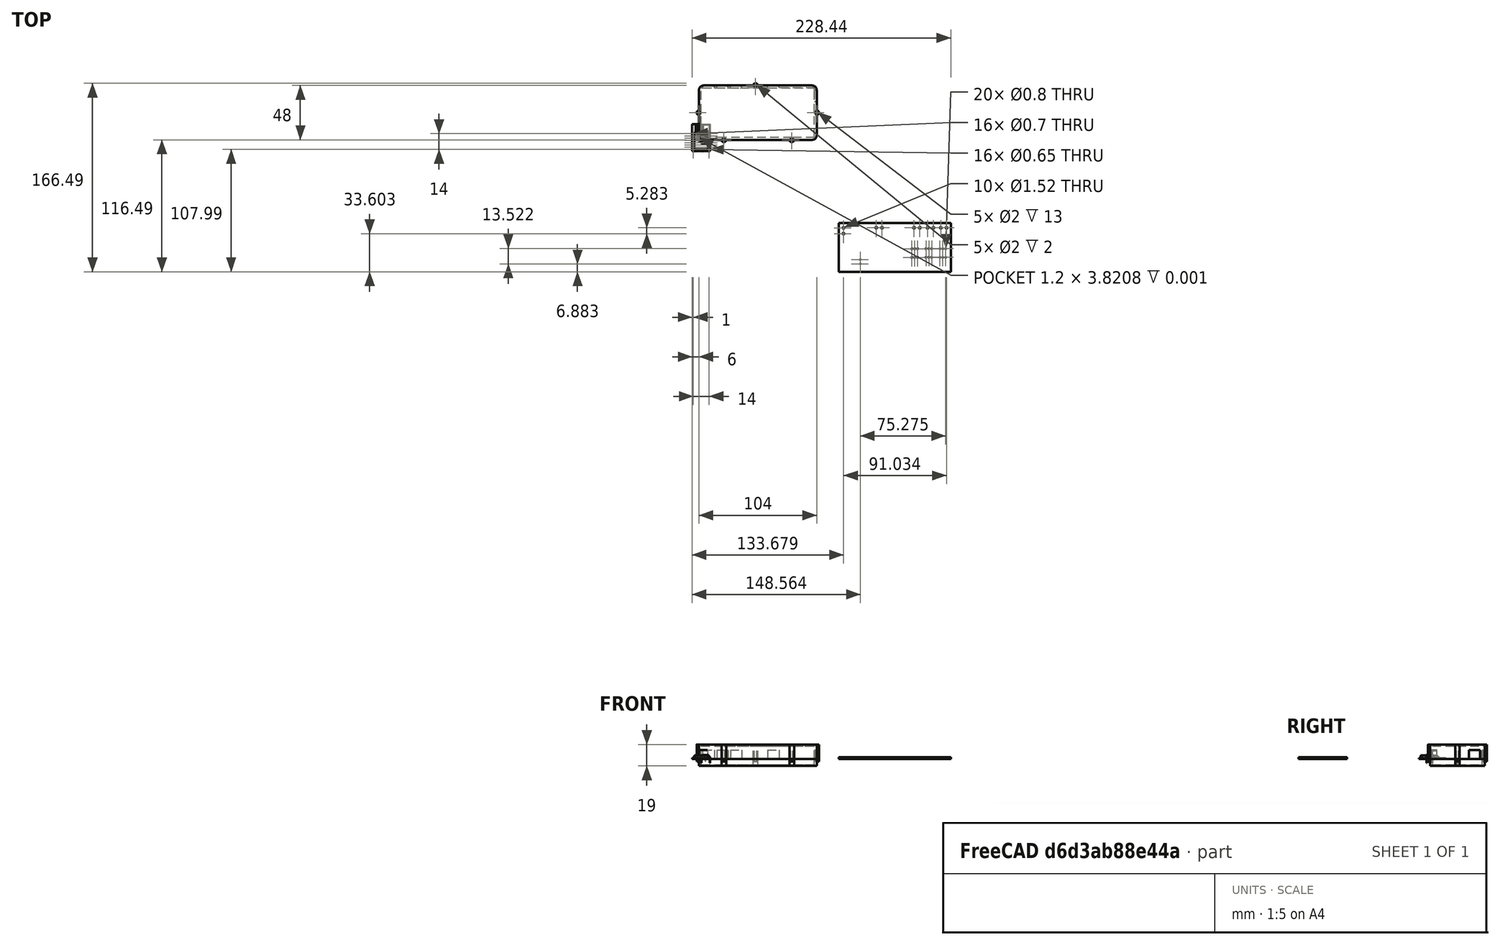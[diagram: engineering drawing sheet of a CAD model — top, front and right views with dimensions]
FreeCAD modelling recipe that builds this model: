
FCSTD DOCUMENT  (FreeCAD 0.20R29603 (Git))
Label: box
License: All rights reserved
LicenseURL: http://en.wikipedia.org/wiki/All_rights_reserved
objects: Part::Feature×44, App::Part×44, Part::Cylinder×25, Part::Box×14, Part::Cut×9, Part::MultiFuse×7, Part::Fillet×2
note: 101 computed .brp shape members not serialized (recipe doc carries the construction recipe); baked Part::Feature solids carry a one-line shape summary decoded from their .brp

FEATURE [Part::Box] Box  label="Куб"
  AttacherType = Attacher::AttachEngine3D
  Height = 16.5
  Length = 100
  Placement = pos=(0,0,-5) rot=(0,0,1;0rad)
  Width = 44
FEATURE [Part::Box] Box001  label="Куб001"
  AttacherType = Attacher::AttachEngine3D
  Height = 8
  Length = 10
  Placement = pos=(1.6,37,0) rot=(0,0,1;0rad)
  Width = 17
FEATURE [Part::Box] Box002  label="Куб002"
  AttacherType = Attacher::AttachEngine3D
  Height = 8
  Length = 10
  Placement = pos=(13.8,37,0) rot=(0,0,1;0rad)
  Width = 17
FEATURE [Part::Box] Box003  label="Куб003"
  AttacherType = Attacher::AttachEngine3D
  Height = 8
  Length = 10
  Placement = pos=(25.8,37,0) rot=(0,0,1;0rad)
  Width = 17
FEATURE [Part::Box] Box004  label="Куб004"
  AttacherType = Attacher::AttachEngine3D
  Height = 8
  Length = 10
  Placement = pos=(58.8,37,0) rot=(0,0,1;0rad)
  Width = 17
FEATURE [Part::Box] Box005  label="Куб005"
  AttacherType = Attacher::AttachEngine3D
  Height = 8
  Length = 10
  Placement = pos=(93.8,42,0) rot=(0,0,-1;1.5708rad)
  Width = 17
FEATURE [Part::MultiFuse] Fusion
  Shapes = -> [Box,Box001,Box002,Box003,Box004,Box005]
FEATURE [Part::Box] Box006  label="Куб006"
  AttacherType = Attacher::AttachEngine3D
  Height = 13
  Length = 104
  Placement = pos=(-2,-2,0) rot=(0,0,1;0rad)
  Width = 48
FEATURE [Part::Box] Box007  label="Куб007"
  AttacherType = Attacher::AttachEngine3D
  Height = 6
  Length = 104
  Placement = pos=(-2,-2,-6) rot=(0,0,1;0rad)
  Width = 48
FEATURE [Part::Box] Box008  label="Куб008"
  AttacherType = Attacher::AttachEngine3D
  Height = 8
  Length = 10
  Placement = pos=(93.8,42,0) rot=(0,0,-1;1.5708rad)
  Width = 17
FEATURE [Part::Box] Box009  label="Куб009"
  AttacherType = Attacher::AttachEngine3D
  Height = 8
  Length = 10
  Placement = pos=(58.8,37,0) rot=(0,0,1;0rad)
  Width = 17
FEATURE [Part::Box] Box010  label="Куб010"
  AttacherType = Attacher::AttachEngine3D
  Height = 8
  Length = 10
  Placement = pos=(13.8,37,0) rot=(0,0,1;0rad)
  Width = 17
FEATURE [Part::Box] Box011  label="Куб011"
  AttacherType = Attacher::AttachEngine3D
  Height = 16.5
  Length = 100
  Placement = pos=(0,0,-5) rot=(0,0,1;0rad)
  Width = 44
FEATURE [Part::Box] Box012  label="Куб012"
  AttacherType = Attacher::AttachEngine3D
  Height = 8
  Length = 10
  Placement = pos=(1.6,37,0) rot=(0,0,1;0rad)
  Width = 17
FEATURE [Part::Box] Box013  label="Куб013"
  AttacherType = Attacher::AttachEngine3D
  Height = 8
  Length = 10
  Placement = pos=(25.8,37,0) rot=(0,0,1;0rad)
  Width = 17
FEATURE [Part::MultiFuse] Fusion001
  Shapes = -> [Box011,Box012,Box010,Box013,Box009,Box008]
FEATURE [Part::Cut] Cut
  Base = -> Box006
  Tool = -> Fusion
FEATURE [Part::Cut] Cut001
  Base = -> Box007
  Tool = -> Fusion001
FEATURE [Part::Fillet] Fillet
  Base = -> Cut
  Edges = 4 edges r=4: [Edge1,Edge3,Edge6,Edge27]
FEATURE [Part::Fillet] Fillet001
  Base = -> Cut001
  Edges = 4 edges r=4: [Edge1,Edge3,Edge6,Edge17]
FEATURE [Part::Cylinder] Cylinder  label="Цилиндр"
  Angle = 360
  AttacherType = Attacher::AttachEngine3D
  FirstAngle = 0
  Height = 13
  Placement = pos=(20,-2,0) rot=(0,0,1;0rad)
  Radius = 2
  SecondAngle = 0
FEATURE [Part::Cylinder] Cylinder001  label="Цилиндр001"
  Angle = 360
  AttacherType = Attacher::AttachEngine3D
  FirstAngle = 0
  Height = 13
  Placement = pos=(80,-2,0) rot=(0,0,1;0rad)
  Radius = 2
  SecondAngle = 0
FEATURE [Part::Cylinder] Cylinder002  label="Цилиндр002"
  Angle = 360
  AttacherType = Attacher::AttachEngine3D
  FirstAngle = 0
  Height = 13
  Placement = pos=(48,46,0) rot=(0,0,1;0rad)
  Radius = 2
  SecondAngle = 0
FEATURE [Part::Cylinder] Cylinder003  label="Цилиндр003"
  Angle = 360
  AttacherType = Attacher::AttachEngine3D
  FirstAngle = 0
  Height = 13
  Placement = pos=(-2,22,0) rot=(0,0,1;0rad)
  Radius = 2
  SecondAngle = 0
FEATURE [Part::Cylinder] Cylinder004  label="Цилиндр004"
  Angle = 360
  AttacherType = Attacher::AttachEngine3D
  FirstAngle = 0
  Height = 13
  Placement = pos=(102,22,0) rot=(0,0,1;0rad)
  Radius = 2
  SecondAngle = 0
FEATURE [Part::Cylinder] Cylinder005  label="Цилиндр005"
  Angle = 360
  AttacherType = Attacher::AttachEngine3D
  FirstAngle = 0
  Height = 13
  Placement = pos=(-2,22,0) rot=(0,0,1;0rad)
  Radius = 1
  SecondAngle = 0
FEATURE [Part::Cylinder] Cylinder006  label="Цилиндр006"
  Angle = 360
  AttacherType = Attacher::AttachEngine3D
  FirstAngle = 0
  Height = 13
  Placement = pos=(20,-2,0) rot=(0,0,1;0rad)
  Radius = 1
  SecondAngle = 0
FEATURE [Part::Cylinder] Cylinder007  label="Цилиндр007"
  Angle = 360
  AttacherType = Attacher::AttachEngine3D
  FirstAngle = 0
  Height = 13
  Placement = pos=(80,-2,0) rot=(0,0,1;0rad)
  Radius = 1
  SecondAngle = 0
FEATURE [Part::Cylinder] Cylinder008  label="Цилиндр008"
  Angle = 360
  AttacherType = Attacher::AttachEngine3D
  FirstAngle = 0
  Height = 13
  Placement = pos=(48,46,0) rot=(0,0,1;0rad)
  Radius = 1
  SecondAngle = 0
FEATURE [Part::Cylinder] Cylinder009  label="Цилиндр009"
  Angle = 360
  AttacherType = Attacher::AttachEngine3D
  FirstAngle = 0
  Height = 13
  Placement = pos=(102,22,0) rot=(0,0,1;0rad)
  Radius = 1
  SecondAngle = 0
FEATURE [Part::Cylinder] Cylinder010  label="Цилиндр010"
  Angle = 360
  AttacherType = Attacher::AttachEngine3D
  FirstAngle = 0
  Height = 13
  Placement = pos=(20,-2,0) rot=(0,0,1;0rad)
  Radius = 1
  SecondAngle = 0
FEATURE [Part::Cylinder] Cylinder011  label="Цилиндр011"
  Angle = 360
  AttacherType = Attacher::AttachEngine3D
  FirstAngle = 0
  Height = 13
  Placement = pos=(80,-2,0) rot=(0,0,1;0rad)
  Radius = 1
  SecondAngle = 0
FEATURE [Part::Cylinder] Cylinder012  label="Цилиндр012"
  Angle = 360
  AttacherType = Attacher::AttachEngine3D
  FirstAngle = 0
  Height = 13
  Placement = pos=(48,46,0) rot=(0,0,1;0rad)
  Radius = 1
  SecondAngle = 0
FEATURE [Part::Cylinder] Cylinder013  label="Цилиндр013"
  Angle = 360
  AttacherType = Attacher::AttachEngine3D
  FirstAngle = 0
  Height = 13
  Placement = pos=(102,22,0) rot=(0,0,1;0rad)
  Radius = 1
  SecondAngle = 0
FEATURE [Part::Cylinder] Cylinder014  label="Цилиндр014"
  Angle = 360
  AttacherType = Attacher::AttachEngine3D
  FirstAngle = 0
  Height = 13
  Placement = pos=(-2,22,0) rot=(0,0,1;0rad)
  Radius = 1
  SecondAngle = 0
FEATURE [Part::MultiFuse] Fusion002
  Shapes = -> [Cylinder,Cylinder001,Cylinder002,Cylinder003,Cylinder004,Fillet]
FEATURE [Part::Cut] Cut002
  Base = -> Fusion002
  Tool = -> Cylinder009
FEATURE [Part::Cut] Cut003
  Base = -> Cut002
  Tool = -> Cylinder005
FEATURE [Part::Cut] Cut004
  Base = -> Cut003
  Tool = -> Cylinder008
FEATURE [Part::Cut] Cut005
  Base = -> Cut004
  Tool = -> Cylinder007
FEATURE [Part::Cut] Cut006
  Base = -> Cut005
  Tool = -> Cylinder006
FEATURE [Part::MultiFuse] Fusion003
  Placement = pos=(0,0,-6) rot=(0,0,1;0rad)
  Shapes = -> [Cylinder010,Cylinder014,Cylinder012,Cylinder013,Cylinder011]
FEATURE [Part::Cylinder] Cylinder015  label="Цилиндр015"
  Angle = 360
  AttacherType = Attacher::AttachEngine3D
  FirstAngle = 0
  Height = 6
  Placement = pos=(20,-2,0) rot=(0,0,1;0rad)
  Radius = 2
  SecondAngle = 0
FEATURE [Part::Cylinder] Cylinder016  label="Цилиндр016"
  Angle = 360
  AttacherType = Attacher::AttachEngine3D
  FirstAngle = 0
  Height = 6
  Placement = pos=(80,-2,0) rot=(0,0,1;0rad)
  Radius = 2
  SecondAngle = 0
FEATURE [Part::Cylinder] Cylinder017  label="Цилиндр017"
  Angle = 360
  AttacherType = Attacher::AttachEngine3D
  FirstAngle = 0
  Height = 6
  Placement = pos=(102,22,0) rot=(0,0,1;0rad)
  Radius = 2
  SecondAngle = 0
FEATURE [Part::Cylinder] Cylinder018  label="Цилиндр018"
  Angle = 360
  AttacherType = Attacher::AttachEngine3D
  FirstAngle = 0
  Height = 6
  Placement = pos=(48,46,0) rot=(0,0,1;0rad)
  Radius = 2
  SecondAngle = 0
FEATURE [Part::Cylinder] Cylinder019  label="Цилиндр019"
  Angle = 360
  AttacherType = Attacher::AttachEngine3D
  FirstAngle = 0
  Height = 6
  Placement = pos=(-2,22,0) rot=(0,0,1;0rad)
  Radius = 2
  SecondAngle = 0
FEATURE [Part::MultiFuse] Fusion004
  Placement = pos=(0,0,-6) rot=(0,0,1;0rad)
  Shapes = -> [Cylinder015,Cylinder019,Cylinder018,Cylinder017,Cylinder016]
FEATURE [Part::Cylinder] Cylinder020  label="Цилиндр020"
  Angle = 360
  AttacherType = Attacher::AttachEngine3D
  FirstAngle = 0
  Height = 6
  Placement = pos=(80,-2,0) rot=(0,0,1;0rad)
  Radius = 2
  SecondAngle = 0
FEATURE [Part::Cylinder] Cylinder021  label="Цилиндр021"
  Angle = 360
  AttacherType = Attacher::AttachEngine3D
  FirstAngle = 0
  Height = 6
  Placement = pos=(20,-2,0) rot=(0,0,1;0rad)
  Radius = 2
  SecondAngle = 0
FEATURE [Part::Cylinder] Cylinder022  label="Цилиндр022"
  Angle = 360
  AttacherType = Attacher::AttachEngine3D
  FirstAngle = 0
  Height = 6
  Placement = pos=(-2,22,0) rot=(0,0,1;0rad)
  Radius = 2
  SecondAngle = 0
FEATURE [Part::Cylinder] Cylinder023  label="Цилиндр023"
  Angle = 360
  AttacherType = Attacher::AttachEngine3D
  FirstAngle = 0
  Height = 6
  Placement = pos=(102,22,0) rot=(0,0,1;0rad)
  Radius = 2
  SecondAngle = 0
FEATURE [Part::Cylinder] Cylinder024  label="Цилиндр024"
  Angle = 360
  AttacherType = Attacher::AttachEngine3D
  FirstAngle = 0
  Height = 6
  Placement = pos=(48,46,0) rot=(0,0,1;0rad)
  Radius = 2
  SecondAngle = 0
FEATURE [Part::MultiFuse] Fusion005
  Placement = pos=(0,0,-8) rot=(0,0,1;0rad)
  Shapes = -> [Cylinder021,Cylinder022,Cylinder024,Cylinder023,Cylinder020]
FEATURE [Part::MultiFuse] Fusion006
  Shapes = -> [Fusion004,Fillet001]
FEATURE [Part::Cut] Cut007
  Base = -> Fusion006
  Tool = -> Fusion003
FEATURE [Part::Cut] Cut008
  Base = -> Cut007
  Tool = -> Fusion005
FEATURE [Part::Feature] Part__Feature043  label="TO-269AA002"
  shape: bbox 6.5 x 4.7 x 1.625 mm, 54 faces (baked)
FEATURE [App::Part] TO_269AA001  label="TO-269AA003"
  Group = -> [Part__Feature043]
  Origin = -> Origin043
  Placement = pos=(127.914,-105.004,1.65) rot=(0,0,1;0rad)
FEATURE [Part::Feature] Part__Feature044  label="R_0805_2012Metric032"
  shape: bbox 2 x 1.2 x 0.45 mm, 26 faces (baked)
FEATURE [App::Part] R_0805_2012Metric016  label="R_0805_2012Metric033"
  Group = -> [Part__Feature044]
  Origin = -> Origin044
  Placement = pos=(155.321,-88.7984,1.65) rot=(0,0,1;3.14159rad)
FEATURE [Part::Feature] Part__Feature045  label="DIP-6_W7.62mm006"
  shape: bbox 7.874 x 7.05 x 6.98 mm, 114 faces (baked)
FEATURE [App::Part] DIP_6_W7_62mm003  label="DIP-6_W7.62mm007"
  Group = -> [Part__Feature045]
  Origin = -> Origin045
  Placement = pos=(186.106,-105.816,1.65) rot=(0,0,1;1.5708rad)
FEATURE [Part::Feature] Part__Feature046  label="R_0805_2012Metric034"
  shape: bbox 2 x 1.2 x 0.45 mm, 26 faces (baked)
FEATURE [App::Part] R_0805_2012Metric017  label="R_0805_2012Metric035"
  Group = -> [Part__Feature046]
  Origin = -> Origin046
  Placement = pos=(195.125,-105.816,1.65) rot=(0,0,1;3.14159rad)
FEATURE [Part::Feature] Part__Feature047  label="R_0805_2012Metric036"
  shape: bbox 2 x 1.2 x 0.45 mm, 26 faces (baked)
FEATURE [App::Part] R_0805_2012Metric018  label="R_0805_2012Metric037"
  Group = -> [Part__Feature047]
  Origin = -> Origin047
  Placement = pos=(182.751,-105.867,1.65) rot=(0,0,1;3.14159rad)
FEATURE [Part::Feature] Part__Feature048  label="R_0805_2012Metric038"
  shape: bbox 2 x 1.2 x 0.45 mm, 26 faces (baked)
FEATURE [App::Part] R_0805_2012Metric019  label="R_0805_2012Metric039"
  Group = -> [Part__Feature048]
  Origin = -> Origin048
  Placement = pos=(148.77,-94.6658,1.65) rot=(0,0,1;0rad)
FEATURE [Part::Feature] Part__Feature049  label="R_0805_2012Metric040"
  shape: bbox 2 x 1.2 x 0.45 mm, 26 faces (baked)
FEATURE [App::Part] R_0805_2012Metric020  label="R_0805_2012Metric041"
  Group = -> [Part__Feature049]
  Origin = -> Origin049
  Placement = pos=(139.749,-86.106,1.65) rot=(0,0,1;0rad)
FEATURE [Part::Feature] Part__Feature050  label="LED_1206_3216Metric008"
  shape: bbox 3.2 x 1.6 x 1.1 mm, 50 faces (baked)
FEATURE [App::Part] LED_1206_3216Metric004  label="LED_1206_3216Metric009"
  Group = -> [Part__Feature050]
  Origin = -> Origin050
  Placement = pos=(213.335,-109.934,1.65) rot=(0,0,-1;1.5708rad)
FEATURE [Part::Feature] Part__Feature051  label="C_1206_3216Metric010"
  shape: bbox 3.2 x 1.6 x 1.6 mm, 28 faces (baked)
FEATURE [App::Part] C_1206_3216Metric005  label="C_1206_3216Metric011"
  Group = -> [Part__Feature051]
  Origin = -> Origin051
  Placement = pos=(186.637,-85.1916,1.65) rot=(0,0,1;3.14159rad)
FEATURE [Part::Feature] Part__Feature052  label="C_1206_3216Metric012"
  shape: bbox 3.2 x 1.6 x 1.6 mm, 28 faces (baked)
FEATURE [App::Part] C_1206_3216Metric006  label="C_1206_3216Metric013"
  Group = -> [Part__Feature052]
  Origin = -> Origin052
  Placement = pos=(198.779,-85.1408,1.65) rot=(0,0,1;3.14159rad)
FEATURE [Part::Feature] Part__Feature053  label="R_0805_2012Metric042"
  shape: bbox 2 x 1.2 x 0.45 mm, 26 faces (baked)
FEATURE [App::Part] R_0805_2012Metric021  label="R_0805_2012Metric043"
  Group = -> [Part__Feature053]
  Origin = -> Origin053
  Placement = pos=(158.344,-91.9461,1.65) rot=(0,0,1;1.5708rad)
FEATURE [Part::Feature] Part__Feature054  label="CP_EIA_7343_31_Kemet_D002"
  shape: bbox 7.3 x 4.627 x 3.1 mm, 46 faces (baked)
FEATURE [App::Part] CP_EIA_7343_31_Kemet_D002  label="CP_EIA-7343-31_Kemet-D002"
  Group = -> [Part__Feature054]
  Origin = -> Origin054
  Placement = pos=(150.952,-107.02,1.65) rot=(0,0,-1;1.5708rad)
FEATURE [Part::Feature] Part__Feature055  label="R_0805_2012Metric044"
  shape: bbox 2 x 1.2 x 0.45 mm, 26 faces (baked)
FEATURE [App::Part] R_0805_2012Metric022  label="R_0805_2012Metric045"
  Group = -> [Part__Feature055]
  Origin = -> Origin055
  Placement = pos=(132.182,-86.2565,1.65) rot=(0,0,-1;1.5708rad)
FEATURE [Part::Feature] Part__Feature056  label="R_0805_2012Metric046"
  shape: bbox 2 x 1.2 x 0.45 mm, 26 faces (baked)
FEATURE [App::Part] R_0805_2012Metric023  label="R_0805_2012Metric047"
  Group = -> [Part__Feature056]
  Origin = -> Origin056
  Placement = pos=(158.293,-96.1663,1.65) rot=(0,0,-1;1.5708rad)
FEATURE [Part::Feature] Part__Feature057  label="LED_1206_3216Metric010"
  shape: bbox 3.2 x 1.6 x 1.1 mm, 50 faces (baked)
FEATURE [App::Part] LED_1206_3216Metric005  label="LED_1206_3216Metric011"
  Group = -> [Part__Feature057]
  Origin = -> Origin057
  Placement = pos=(201.092,-109.96,1.65) rot=(0,0,-1;1.5708rad)
FEATURE [Part::Feature] Part__Feature058  label="C_1206_3216Metric014"
  shape: bbox 3.2 x 1.6 x 1.6 mm, 28 faces (baked)
FEATURE [App::Part] C_1206_3216Metric007  label="C_1206_3216Metric015"
  Group = -> [Part__Feature058]
  Origin = -> Origin058
  Placement = pos=(211.631,-85.1916,1.65) rot=(0,0,1;3.14159rad)
FEATURE [Part::Feature] Part__Feature059  label="CQ assembly003"
  shape: bbox 9.9 x 6.5 x 2.32 mm, 83 faces, 5 solids (baked)
FEATURE [App::Part] TO_252_2003  label="TO-252-005"
  Group = -> [Part__Feature059]
  Origin = -> Origin059
  Placement = pos=(188.149,-91.7,1.65) rot=(0,0,1;0rad)
FEATURE [Part::Feature] Part__Feature060  label="R_1206_3216Metric008"
  shape: bbox 3.2 x 1.6 x 0.55 mm, 26 faces (baked)
FEATURE [App::Part] R_1206_3216Metric004  label="R_1206_3216Metric009"
  Group = -> [Part__Feature060]
  Origin = -> Origin060
  Placement = pos=(125.832,-92.2421,1.65) rot=(0,0,-1;1.5708rad)
FEATURE [Part::Feature] Part__Feature061  label="C_1206_3216Metric016"
  shape: bbox 3.2 x 1.6 x 1.6 mm, 28 faces (baked)
FEATURE [App::Part] C_1206_3216Metric008  label="C_1206_3216Metric017"
  Group = -> [Part__Feature061]
  Origin = -> Origin061
  Placement = pos=(132.029,-80.8718,1.65) rot=(0,0,-1;1.5708rad)
FEATURE [Part::Feature] Part__Feature062  label="R_1206_3216Metric010"
  shape: bbox 3.2 x 1.6 x 0.55 mm, 26 faces (baked)
FEATURE [App::Part] R_1206_3216Metric005  label="R_1206_3216Metric011"
  Group = -> [Part__Feature062]
  Origin = -> Origin062
  Placement = pos=(191.73,-85.1408,1.65) rot=(0,0,1;3.14159rad)
FEATURE [Part::Feature] Part__Feature063  label="R_0805_2012Metric048"
  shape: bbox 2 x 1.2 x 0.45 mm, 26 faces (baked)
FEATURE [App::Part] R_0805_2012Metric024  label="R_0805_2012Metric049"
  Group = -> [Part__Feature063]
  Origin = -> Origin063
  Placement = pos=(207.34,-97.1061,1.65) rot=(0,0,1;1.5708rad)
FEATURE [Part::Feature] Part__Feature064  label="R_0805_2012Metric050"
  shape: bbox 2 x 1.2 x 0.45 mm, 26 faces (baked)
FEATURE [App::Part] R_0805_2012Metric025  label="R_0805_2012Metric051"
  Group = -> [Part__Feature064]
  Origin = -> Origin064
  Placement = pos=(207.266,-111.277,1.65) rot=(0,0,1;0rad)
FEATURE [Part::Feature] Part__Feature065  label="D_MELF_Standard002"
  shape: bbox 5.8 x 2.2 x 2.2 mm, 13 faces (baked)
FEATURE [App::Part] D_MELF002
  Group = -> [Part__Feature065]
  Origin = -> Origin065
  Placement = pos=(135.954,-96.3168,1.65) rot=(0,0,1;0rad)
FEATURE [Part::Feature] Part__Feature066  label="CQ assembly004"
  shape: bbox 9.9 x 6.5 x 2.32 mm, 83 faces, 5 solids (baked)
FEATURE [App::Part] TO_252_2004  label="TO-252-006"
  Group = -> [Part__Feature066]
  Origin = -> Origin066
  Placement = pos=(200.391,-91.7,1.65) rot=(0,0,1;0rad)
FEATURE [Part::Feature] Part__Feature067  label="R_1206_3216Metric012"
  shape: bbox 3.2 x 1.6 x 0.55 mm, 26 faces (baked)
FEATURE [App::Part] R_1206_3216Metric006  label="R_1206_3216Metric013"
  Group = -> [Part__Feature067]
  Origin = -> Origin067
  Placement = pos=(216.622,-85.09,1.65) rot=(0,0,1;3.14159rad)
FEATURE [Part::Feature] Part__Feature068  label="R_0805_2012Metric052"
  shape: bbox 2 x 1.2 x 0.45 mm, 26 faces (baked)
FEATURE [App::Part] R_0805_2012Metric026  label="R_0805_2012Metric053"
  Group = -> [Part__Feature068]
  Origin = -> Origin068
  Placement = pos=(182.778,-97.0261,1.65) rot=(0,0,1;1.5708rad)
FEATURE [Part::Feature] Part__Feature069  label="CP_EIA_7343_31_Kemet_D003"
  shape: bbox 7.3 x 4.627 x 3.1 mm, 46 faces (baked)
FEATURE [App::Part] CP_EIA_7343_31_Kemet_D003  label="CP_EIA-7343-31_Kemet-D003"
  Group = -> [Part__Feature069]
  Origin = -> Origin069
  Placement = pos=(135.671,-90.5764,1.65) rot=(0,0,1;0rad)
FEATURE [Part::Feature] Part__Feature070  label="R_1206_3216Metric014"
  shape: bbox 3.2 x 1.6 x 0.55 mm, 26 faces (baked)
FEATURE [App::Part] R_1206_3216Metric007  label="R_1206_3216Metric015"
  Group = -> [Part__Feature070]
  Origin = -> Origin070
  Placement = pos=(204.074,-85.09,1.65) rot=(0,0,1;3.14159rad)
FEATURE [Part::Feature] Part__Feature071  label="LED_1206_3216Metric012"
  shape: bbox 3.2 x 1.6 x 1.1 mm, 50 faces (baked)
FEATURE [App::Part] LED_1206_3216Metric006  label="LED_1206_3216Metric013"
  Group = -> [Part__Feature071]
  Origin = -> Origin071
  Placement = pos=(143.866,-97.9648,1.65) rot=(0,0,1;1.5708rad)
FEATURE [Part::Feature] Part__Feature072  label="R_1206_3216Metric016"
  shape: bbox 3.2 x 1.6 x 0.55 mm, 26 faces (baked)
FEATURE [App::Part] R_1206_3216Metric008  label="R_1206_3216Metric017"
  Group = -> [Part__Feature072]
  Origin = -> Origin072
  Placement = pos=(146.202,-103.744,1.65) rot=(0,0,-1;1.5708rad)
FEATURE [Part::Feature] Part__Feature073  label="CP_Radial_D80mm_P380mm001"
  shape: bbox 9.886 x 10.23 x 10 mm, 54 faces (baked)
FEATURE [App::Part] CP_Radial_D8_0mm_P3_80mm001  label="CP_Radial_D8.0mm_P3.80mm001"
  Group = -> [Part__Feature073]
  Origin = -> Origin073
  Placement = pos=(140.564,-111.607,1.65) rot=(0,0,1;1.5708rad)
FEATURE [Part::Feature] Part__Feature074  label="CQ assembly005"
  shape: bbox 9.9 x 6.5 x 2.32 mm, 83 faces, 5 solids (baked)
FEATURE [App::Part] TO_252_2005  label="TO-252-007"
  Group = -> [Part__Feature074]
  Origin = -> Origin074
  Placement = pos=(212.657,-91.7184,1.65) rot=(0,0,1;0rad)
FEATURE [Part::Feature] Part__Feature075  label="R_0805_2012Metric054"
  shape: bbox 2 x 1.2 x 0.45 mm, 26 faces (baked)
FEATURE [App::Part] R_0805_2012Metric027  label="R_0805_2012Metric055"
  Group = -> [Part__Feature075]
  Origin = -> Origin075
  Placement = pos=(147.775,-99.314,1.65) rot=(0,0,1;3.14159rad)
FEATURE [Part::Feature] Part__Feature076  label="R_0805_2012Metric056"
  shape: bbox 2 x 1.2 x 0.45 mm, 26 faces (baked)
FEATURE [App::Part] R_0805_2012Metric028  label="R_0805_2012Metric057"
  Group = -> [Part__Feature076]
  Origin = -> Origin076
  Placement = pos=(195.123,-97.0007,1.65) rot=(0,0,1;1.5708rad)
FEATURE [Part::Feature] Part__Feature077  label="DIP-6_W7.62mm008"
  shape: bbox 7.874 x 7.05 x 6.98 mm, 114 faces (baked)
FEATURE [App::Part] DIP_6_W7_62mm004  label="DIP-6_W7.62mm009"
  Group = -> [Part__Feature077]
  Origin = -> Origin077
  Placement = pos=(198.541,-105.781,1.65) rot=(0,0,1;1.5708rad)
FEATURE [Part::Feature] Part__Feature078  label="C_1206_3216Metric018"
  shape: bbox 3.2 x 1.6 x 1.6 mm, 28 faces (baked)
FEATURE [App::Part] C_1206_3216Metric009  label="C_1206_3216Metric019"
  Group = -> [Part__Feature078]
  Origin = -> Origin078
  Placement = pos=(155.497,-85.4456,1.65) rot=(0,0,1;0rad)
FEATURE [Part::Feature] Part__Feature079  label="DIP-6_W7.62mm010"
  shape: bbox 7.874 x 7.05 x 6.98 mm, 114 faces (baked)
FEATURE [App::Part] DIP_6_W7_62mm005  label="DIP-6_W7.62mm011"
  Group = -> [Part__Feature079]
  Origin = -> Origin079
  Placement = pos=(210.759,-105.705,1.65) rot=(0,0,1;1.5708rad)
FEATURE [Part::Feature] Part__Feature080  label="R_0805_2012Metric058"
  shape: bbox 2 x 1.2 x 0.45 mm, 26 faces (baked)
FEATURE [App::Part] R_0805_2012Metric029  label="R_0805_2012Metric059"
  Group = -> [Part__Feature080]
  Origin = -> Origin080
  Placement = pos=(207.24,-105.766,1.65) rot=(0,0,1;3.14159rad)
FEATURE [Part::Feature] Part__Feature081  label="D_MELF_Standard003"
  shape: bbox 5.8 x 2.2 x 2.2 mm, 13 faces (baked)
FEATURE [App::Part] D_MELF003
  Group = -> [Part__Feature081]
  Origin = -> Origin081
  Placement = pos=(145.53,-79.8576,1.65) rot=(0,0,1;0rad)
FEATURE [Part::Feature] Part__Feature082  label="R_0805_2012Metric060"
  shape: bbox 2 x 1.2 x 0.45 mm, 26 faces (baked)
FEATURE [App::Part] R_0805_2012Metric030  label="R_0805_2012Metric061"
  Group = -> [Part__Feature082]
  Origin = -> Origin082
  Placement = pos=(182.78,-111.1,1.65) rot=(0,0,1;0rad)
FEATURE [Part::Feature] Part__Feature083  label="ESP_12E001_cp001"
  shape: bbox 16 x 24 x 3.2 mm, 488 faces, 48 solids (baked)
FEATURE [App::Part] ESP_12E001  label="ESP-12E001"
  Group = -> [Part__Feature083]
  Origin = -> Origin083
  Placement = pos=(170.942,-97.8408,1.65) rot=(0,0,1;0rad)
FEATURE [Part::Feature] Part__Feature084  label="R_0805_2012Metric062"
  shape: bbox 2 x 1.2 x 0.45 mm, 26 faces (baked)
FEATURE [App::Part] R_0805_2012Metric031  label="R_0805_2012Metric063"
  Group = -> [Part__Feature084]
  Origin = -> Origin084
  Placement = pos=(195.277,-111.201,1.65) rot=(0,0,1;0rad)
FEATURE [Part::Feature] Part__Feature085  label="LED_1206_3216Metric014"
  shape: bbox 3.2 x 1.6 x 1.1 mm, 50 faces (baked)
FEATURE [App::Part] LED_1206_3216Metric007  label="LED_1206_3216Metric015"
  Group = -> [Part__Feature085]
  Origin = -> Origin085
  Placement = pos=(188.519,-109.934,1.65) rot=(0,0,-1;1.5708rad)
FEATURE [Part::Feature] Part__Feature086  label="light_switch_controller_PCB001"
  shape: bbox 99 x 43 x 1.6 mm, 36 faces (baked)
FEATURE [App::Part] light_switch_controller_1001  label="light_switch_controller 002"
  Group = -> [TO_269AA001,R_0805_2012Metric016,DIP_6_W7_62mm003,R_0805_2012Metric017,R_0805_2012Metric018,R_0805_2012Metric019,R_0805_2012Metric020,LED_1206_3216Metric004,C_1206_3216Metric005,C_1206_3216Metric006,R_0805_2012Metric021,CP_EIA_7343_31_Kemet_D002,R_0805_2012Metric022,R_0805_2012Metric023,LED_1206_3216Metric005,C_1206_3216Metric007,TO_252_2003,R_1206_3216Metric004,C_1206_3216Metric008,+25 more]
  Origin = -> Origin086
  Placement = pos=(221,119,11) rot=(0,1,0;3.14159rad)
